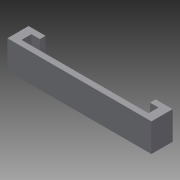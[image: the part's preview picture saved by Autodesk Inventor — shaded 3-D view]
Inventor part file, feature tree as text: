
AUTODESK INVENTOR PART (.ipt)
format: ipt  version: 2015 (Build 190159000, 159)  size: 89,088 bytes
history: native  units: mm
features: extrude x1, sketch x1
ambient origin geometry x8: Origin, YZ Plane, XZ Plane, XY Plane, X Axis, Y Axis, Z Axis, Center Point
bodies: Solid1 (feature_tree)
feature tree (2):
  extrude  "Extrusion1"  Depth=3.5mm
  sketch  "Sketch1"  dims[d0=45.0mm d1=3.5mm d2=6.0mm d3=6.0mm d4=51.0mm d5=3.0mm d6=2.0mm d7=3.0mm d8=2.0mm d9=2.0mm d10=10.0mm d11=0.0mm]
